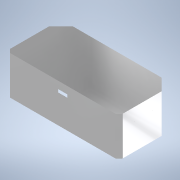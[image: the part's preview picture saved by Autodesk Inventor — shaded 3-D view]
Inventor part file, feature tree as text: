
AUTODESK INVENTOR PART (.ipt)
format: ipt  version: 2022.1 (Build 261234000, 234)  size: 299,008 bytes
history: native  units: mm
features: reference x16, other x10, sketch x5, extrude x2, hole x2, projected_geometry x2, plane x1
ambient origin geometry x8: Origin, YZ Plane, XZ Plane, XY Plane, X Axis, Y Axis, Z Axis, Center Point
bodies: Body1 (feature_tree)
feature tree (38):
  other  "Sólido1"
  plane  "Plano de trabajo1"
  extrude  "Extrusión1"  Depth=1.5mm TaperAngle=0.0deg
  extrude  "Extrusión2"  Depth=5.0mm
  hole  "Agujero1"  [1 undecoded]
  hole  "Agujero2"  [1 undecoded]
  sketch  "Boceto16"  dims[d10=2.459mm d11=6.0mm d12=10.4mm d13=2.0mm d14=90.0deg d15=8.8mm d16=20.594885mm d21=5.0mm]
  sketch  "Boceto17"  dims[d23=100.0mm d24=100.0mm d26=2.459mm d27=6.0mm d28=4.0mm d29=2.0mm d30=90.0deg d31=8.0mm d32=20.594885mm d63=1.5mm d65=80.0mm d69=80.0mm d70=80.0mm d71=70.0mm d72=30.0mm d73=90.0mm d76=5.0mm d77=5.0mm d78=5.0mm d79=5.0mm d80=1.5mm d81=1.5mm d82=0.0mm d83=1.5mm d84=0.0mm d86=20.0mm d87=121.5mm d88=121.5mm d89=121.5mm d90=80.0mm d92=308.22078mm d93=308.519149mm]
  reference  "Referencia1"
  reference  "Referencia2"
  reference  "Referencia3"
  reference  "Referencia4"
  reference  "Referencia5"
  reference  "Referencia6"
  reference  "Referencia7"
  reference  "Referencia8"
  sketch  "Boceto2"  dims[d1=371.581mm d2=0.0mm d3=1.5mm d4=0.0mm]
  projected_geometry  "Contorno proyectado1"
  sketch  "Boceto4"  dims[d7=5.0mm d8=200.0mm]
  reference  "Referencia9"
  sketch  "Boceto7"  dims[d9=200.0mm]
  reference  "Referencia10"
  reference  "Referencia11"
  reference  "Referencia12"
  reference  "Referencia13"
  reference  "Referencia14"
  reference  "Referencia15"
  reference  "Referencia16"
  projected_geometry  "Contorno proyectado4"
  other  "Cortar1"
  other  "Cortar2"
  other  "<userpath>\Desktop\PDM\ProyectoRobotPallet\RobotPallet.iam"
  other  "RobotPallet.iam"
  other  "CubieraInferior:1"
  other  "EstructuraInferior:1"
  other  "Frame_Base:1"
  other  "ISO 10799-2 40x40x2 - 2899.41:1"
  other  "ISO 10799-2 40x40x2 - 325.18:3"
note: 2 required parameter values undecoded (feature->parameter linkage not recoverable at this tier; creation-order binding heuristic only, values carry confidence <= 0.55)
